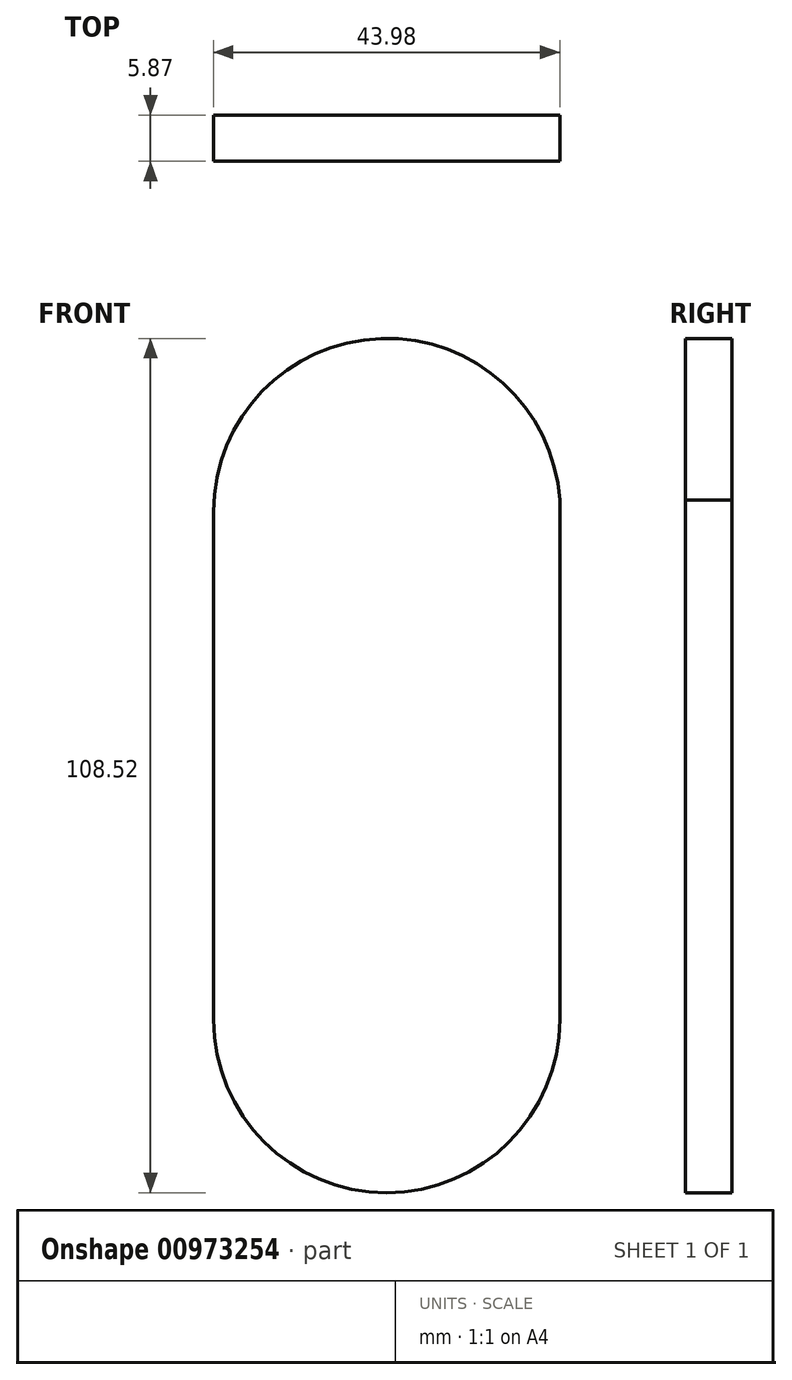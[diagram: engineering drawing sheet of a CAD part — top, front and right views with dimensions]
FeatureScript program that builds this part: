
annotation { "Feature Type Name" : "Feature", "Feature Type Description" : "" }
export const myFeature = defineFeature(function(context is Context, id is Id, definition is map)
    precondition{}
    {
        {
            var Q0;
            Q0=qCreatedBy(makeId("Front.planeOp"),FACE);
            var sketch = newSketch(context, id + "F0", { "sketchPlane" : qUnion([Q0])});
            skLineSegment(sketch, "E0", {"start": v(11.41, 64.52) * mm, "end": v(11.41, 0) * mm});
            skArc(sketch, "E1", {"start": v(11.41, 0) * mm, "mid": v(33.4, -22) * mm, "end": v(55.4, 0) * mm});
            skLineSegment(sketch, "E2", {"start": v(55.4, 0) * mm, "end": v(55.4, 65.97) * mm});
            skArc(sketch, "E3", {"start": v(11.41, 64.52) * mm, "mid": v(32.7, 86.52) * mm, "end": v(55.4, 65.97) * mm});
            skSolve(sketch);
        }
        {
            var Q0;
            Q0 = qSketchRegion(id + "F0", true);
            extrude(context, id + "F1", {"entities" : qUnion([Q0]), "depth" : 5.87 * mm, "offsetDistance" : 25.4 * mm});
        }
    });
